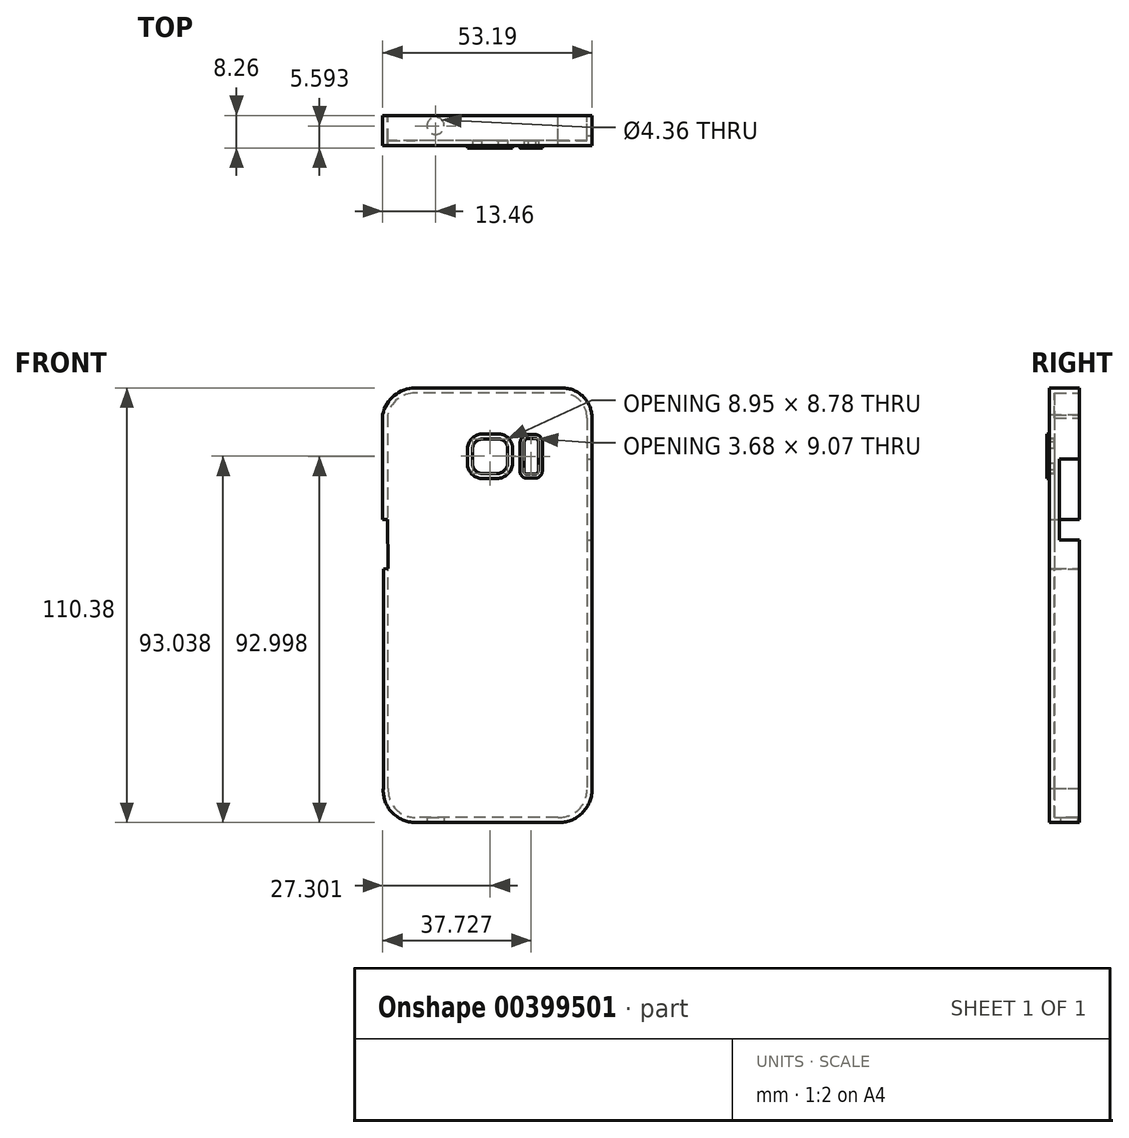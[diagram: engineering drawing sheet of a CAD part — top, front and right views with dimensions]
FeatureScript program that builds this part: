
annotation { "Feature Type Name" : "Feature", "Feature Type Description" : "" }
export const myFeature = defineFeature(function(context is Context, id is Id, definition is map)
    precondition{}
    {
        {
            var Q0;
            Q0=qCreatedBy(makeId("Front.planeOp"),FACE);
            var sketch = newSketch(context, id + "F0", { "sketchPlane" : qUnion([Q0])});
            skLineSegment(sketch, "E0", {"start": v(31.91, 44.57) * mm, "end": v(31.91, 34.16) * mm});
            skLineSegment(sketch, "E1", {"start": v(31.92, 13.5) * mm, "end": v(31.92, -49.87) * mm});
            skLineSegment(sketch, "E2", {"start": v(23.27, -58.16) * mm, "end": v(-12.99, -58.16) * mm});
            skLineSegment(sketch, "E3", {"start": v(-21.1, -49.5) * mm, "end": v(-21.1, 6.28) * mm});
            skLineSegment(sketch, "E4", {"start": v(24.35, 52.21) * mm, "end": v(-12.99, 52.21) * mm});
            skLineSegment(sketch, "E5", {"start": v(-21.27, 45.42) * mm, "end": v(-21.27, 18.78) * mm});
            skArc(sketch, "E6", {"start": v(24.35, 52.21) * mm, "mid": v(29.72, 49.97) * mm, "end": v(31.91, 44.57) * mm});
            skArc(sketch, "E7", {"start": v(-12.99, 52.21) * mm, "mid": v(-18.34, 50.3) * mm, "end": v(-21.27, 45.42) * mm});
            skArc(sketch, "E8", {"start": v(31.92, -49.87) * mm, "mid": v(29.36, -55.86) * mm, "end": v(23.27, -58.16) * mm});
            skArc(sketch, "E9", {"start": v(-12.99, -58.16) * mm, "mid": v(-18.92, -55.6) * mm, "end": v(-21.1, -49.5) * mm});
            skLineSegment(sketch, "E10", {"start": v(31.91, 34.16) * mm, "end": v(34.2, 34.16) * mm});
            skLineSegment(sketch, "E11.0", {"start": v(34.2, 44.56) * mm, "end": v(34.2, 34.16) * mm});
            skArc(sketch, "E11.1", {"start": v(24.35, 54.5) * mm, "mid": v(31.34, 51.58) * mm, "end": v(34.2, 44.56) * mm});
            skLineSegment(sketch, "E11.2", {"start": v(24.35, 54.5) * mm, "end": v(-12.99, 54.5) * mm});
            skArc(sketch, "E11.3", {"start": v(-12.99, 54.5) * mm, "mid": v(-19.88, 51.99) * mm, "end": v(-23.56, 45.64) * mm});
            skLineSegment(sketch, "E11.4", {"start": v(-23.56, 45.64) * mm, "end": v(-23.56, 18.78) * mm});
            skLineSegment(sketch, "E11.5", {"start": v(-21.27, 18.78) * mm, "end": v(-23.56, 18.78) * mm});
            skLineSegment(sketch, "E11.9", {"start": v(34.73, 24.26) * mm, "end": v(34.71, 24.26) * mm});
            skLineSegment(sketch, "E11.11", {"start": v(34.2, 13.5) * mm, "end": v(34.2, -49.87) * mm});
            skArc(sketch, "E11.12", {"start": v(34.2, -49.87) * mm, "mid": v(30.96, -57.5) * mm, "end": v(23.22, -60.45) * mm});
            skLineSegment(sketch, "E11.13", {"start": v(23.22, -60.45) * mm, "end": v(-12.99, -60.45) * mm});
            skArc(sketch, "E11.14", {"start": v(-12.99, -60.45) * mm, "mid": v(-20.56, -57.18) * mm, "end": v(-23.39, -49.43) * mm});
            skLineSegment(sketch, "E11.15", {"start": v(-23.39, -49.43) * mm, "end": v(-23.39, 6.28) * mm});
            skLineSegment(sketch, "E11.16", {"start": v(-23.39, 6.28) * mm, "end": v(-21.1, 6.28) * mm});
            skPoint(sketch, "E12.start.orphan", {"position": v(32.43, 15.78) * mm});
            skLineSegment(sketch, "E13", {"start": v(34.2, 13.5) * mm, "end": v(31.92, 13.5) * mm});
            skPoint(sketch, "E14.orphan", {"position": v(31.92, 15.78) * mm});
            skLineSegment(sketch, "E15", {"start": v(-23.56, 18.78) * mm, "end": v(-23.39, 6.28) * mm});
            skLineSegment(sketch, "E16", {"start": v(-21.27, 18.78) * mm, "end": v(-21.1, 6.28) * mm});
            skLineSegment(sketch, "E17", {"start": v(34.2, 34.16) * mm, "end": v(34.2, 13.5) * mm});
            skLineSegment(sketch, "E18", {"start": v(31.91, 34.16) * mm, "end": v(31.92, 13.5) * mm});
            skLineSegment(sketch, "E19", {"start": v(38.67, 39.3) * mm, "end": v(38.67, -10.21) * mm});
            skLineSegment(sketch, "E20", {"start": v(40.23, -10.83) * mm, "end": v(40.23, -26.24) * mm});
            skLineSegment(sketch, "E21", {"start": v(38.67, -10.21) * mm, "end": v(40.23, -10.83) * mm});
            skLineSegment(sketch, "E22", {"start": v(40.23, -26.24) * mm, "end": v(44.59, -30.44) * mm});
            skLineSegment(sketch, "E23", {"start": v(44.59, -30.44) * mm, "end": v(41.47, -62.98) * mm});
            skLineSegment(sketch, "E24", {"start": v(41.47, -62.98) * mm, "end": v(38.67, -62.98) * mm});
            skLineSegment(sketch, "E25", {"start": v(38.67, -62.98) * mm, "end": v(36.5, -64.85) * mm});
            skLineSegment(sketch, "E26", {"start": v(36.5, -64.85) * mm, "end": v(5.61, -64.85) * mm});
            skLineSegment(sketch, "E27", {"start": v(38.67, 39.3) * mm, "end": v(36.72, 49.13) * mm});
            skLineSegment(sketch, "E28", {"start": v(36.72, 49.13) * mm, "end": v(35, 49.13) * mm});
            skLineSegment(sketch, "E29.MirrorCS", {"start": v(-27.44, -62.98) * mm, "end": v(-25.26, -64.85) * mm});
            skLineSegment(sketch, "E30.MirrorCS", {"start": v(-30.25, -62.98) * mm, "end": v(-27.44, -62.98) * mm});
            skLineSegment(sketch, "E31.MirrorCS", {"start": v(-29, -26.24) * mm, "end": v(-33.36, -30.44) * mm});
            skLineSegment(sketch, "E32.MirrorCS", {"start": v(-27.44, 39.3) * mm, "end": v(-25.5, 49.13) * mm});
            skLineSegment(sketch, "E33.MirrorCS", {"start": v(-27.44, -10.21) * mm, "end": v(-29, -10.83) * mm});
            skLineSegment(sketch, "E34.MirrorCS", {"start": v(-25.5, 49.13) * mm, "end": v(-23.77, 49.13) * mm});
            skLineSegment(sketch, "E35.MirrorCS", {"start": v(-33.36, -30.44) * mm, "end": v(-30.25, -62.98) * mm});
            skLineSegment(sketch, "E36.MirrorCS", {"start": v(-27.44, 39.3) * mm, "end": v(-27.44, -10.21) * mm});
            skLineSegment(sketch, "E37.MirrorCS", {"start": v(-29, -10.83) * mm, "end": v(-29, -26.24) * mm});
            skLineSegment(sketch, "E38.MirrorCS", {"start": v(-25.26, -64.85) * mm, "end": v(5.61, -64.85) * mm});
            skSolve(sketch);
        }
        {
            var Q0;
            Q0=makeQuery(id+"F0.imprint","IMPRINT",FACE,{"disambiguationData":[TD([[makeQuery(id+"F0.imprint","IMPRINT",EDGE,{"derivedFrom":sQuery(id+"F0.wireOp",EDGE,"E0")}),-1.0]])]});
            extrude(context, id + "F1", {"entities" : qUnion([Q0]), "depth" : 7.62 * mm});
        }
        {
            var Q0;
            Q0=makeQuery(id+"F1.opExtrude","CAP_FACE",FACE,{"disambiguationData":[OSD([sQuery(id+"F0.wireOp",EDGE,"E0"),sQuery(id+"F0.wireOp",EDGE,"E1"),sQuery(id+"F0.wireOp",EDGE,"E2"),sQuery(id+"F0.wireOp",EDGE,"E3"),sQuery(id+"F0.wireOp",EDGE,"E4"),sQuery(id+"F0.wireOp",EDGE,"E5"),sQuery(id+"F0.wireOp",EDGE,"E6"),sQuery(id+"F0.wireOp",EDGE,"E7"),sQuery(id+"F0.wireOp",EDGE,"E8"),sQuery(id+"F0.wireOp",EDGE,"E9"),sQuery(id+"F0.wireOp",EDGE,"bb75414d-56e8-4ebf-947c-b1fa3df4ddbe.0"),sQuery(id+"F0.wireOp",EDGE,"bb75414d-56e8-4ebf-947c-b1fa3df4ddbe.1"),sQuery(id+"F0.wireOp",EDGE,"bb75414d-56e8-4ebf-947c-b1fa3df4ddbe.2"),sQuery(id+"F0.wireOp",EDGE,"bb75414d-56e8-4ebf-947c-b1fa3df4ddbe.3"),sQuery(id+"F0.wireOp",EDGE,"bb75414d-56e8-4ebf-947c-b1fa3df4ddbe.4"),sQuery(id+"F0.wireOp",EDGE,"bb75414d-56e8-4ebf-947c-b1fa3df4ddbe.5"),sQuery(id+"F0.wireOp",EDGE,"bb75414d-56e8-4ebf-947c-b1fa3df4ddbe.6"),sQuery(id+"F0.wireOp",EDGE,"bb75414d-56e8-4ebf-947c-b1fa3df4ddbe.7"),sQuery(id+"F0.wireOp",EDGE,"35a4204d-8211-4e34-a5d2-bb70df10542c.0"),sQuery(id+"F0.wireOp",EDGE,"35a4204d-8211-4e34-a5d2-bb70df10542c.1"),sQuery(id+"F0.wireOp",EDGE,"35a4204d-8211-4e34-a5d2-bb70df10542c.2"),sQuery(id+"F0.wireOp",EDGE,"35a4204d-8211-4e34-a5d2-bb70df10542c.3"),sQuery(id+"F0.wireOp",EDGE,"35a4204d-8211-4e34-a5d2-bb70df10542c.4"),sQuery(id+"F0.wireOp",EDGE,"35a4204d-8211-4e34-a5d2-bb70df10542c.5"),sQuery(id+"F0.wireOp",EDGE,"35a4204d-8211-4e34-a5d2-bb70df10542c.6"),sQuery(id+"F0.wireOp",EDGE,"35a4204d-8211-4e34-a5d2-bb70df10542c.7"),sQuery(id+"F0.wireOp",EDGE,"E16"),sQuery(id+"F0.wireOp",EDGE,"E18")])],"isStart":true});
            shell(context, id + "F2", {"entities" : qUnion([Q0]), "thickness" : 1.27 * mm});
        }
        {
            var Q0;
            Q0=makeQuery(id+"F1.opExtrude","SWEPT_FACE",FACE,{"disambiguationData":[OSD([sQuery(id+"F0.wireOp",EDGE,"E16")])]});
            cPlane(context, id + "F3", {"entities" : qUnion([Q0]), "cplaneType" : CPlaneType.OFFSET, "offset" : 0 * mm, "width" : 152.4 * mm, "height" : 152.4 * mm});
        }
        {
            var Q0;
            Q0=makeQuery(id+"F1.opExtrude","SWEPT_FACE",FACE,{"disambiguationData":[OSD([sQuery(id+"F0.wireOp",EDGE,"E16")])]});
            extrude(context, id + "F4", {"entities" : qUnion([Q0]), "operationType" : NewBodyOperationType.REMOVE, "oppositeDirection" : true, "depth" : 1.27 * mm});
        }
        {
            var Q0;
            Q0=makeQuery(id+"F1.opExtrude","SWEPT_FACE",FACE,{"disambiguationData":[OSD([sQuery(id+"F0.wireOp",EDGE,"E18")])]});
            cPlane(context, id + "F5", {"entities" : qUnion([Q0]), "cplaneType" : CPlaneType.OFFSET, "offset" : 0 * mm, "width" : 152.4 * mm, "height" : 152.4 * mm});
        }
        {
            var Q0;
            Q0=qCreatedBy(id+"F5.planeOp",FACE);
            var sketch = newSketch(context, id + "F6", { "sketchPlane" : qUnion([Q0])});
            skLineSegment(sketch, "E39.bottom", {"start": v(-5.1, 34.2) * mm, "end": v(0, 34.2) * mm});
            skLineSegment(sketch, "E39.top", {"start": v(-5.1, 13.52) * mm, "end": v(0, 13.52) * mm});
            skLineSegment(sketch, "E39.left", {"start": v(-5.1, 34.2) * mm, "end": v(-5.1, 13.52) * mm});
            skLineSegment(sketch, "E39.right", {"start": v(0, 34.2) * mm, "end": v(0, 13.52) * mm});
            skSolve(sketch);
        }
        {
            var Q0;
            Q0=makeQuery(id+"F6.imprint","IMPRINT",FACE,{"disambiguationData":[TD([[makeQuery(id+"F6.imprint","IMPRINT",EDGE,{"derivedFrom":sQuery(id+"F6.wireOp",EDGE,"E39.bottom")}),-1.0]])]});
            extrude(context, id + "F7", {"entities" : qUnion([Q0]), "operationType" : NewBodyOperationType.REMOVE, "oppositeDirection" : true, "depth" : 1.27 * mm});
        }
        {
            var Q0;
            Q0=makeQuery(id+"F1.opExtrude","CAP_FACE",FACE,{"disambiguationData":[OSD([sQuery(id+"F0.wireOp",EDGE,"E0"),sQuery(id+"F0.wireOp",EDGE,"E1"),sQuery(id+"F0.wireOp",EDGE,"E2"),sQuery(id+"F0.wireOp",EDGE,"E3"),sQuery(id+"F0.wireOp",EDGE,"E4"),sQuery(id+"F0.wireOp",EDGE,"E5"),sQuery(id+"F0.wireOp",EDGE,"E6"),sQuery(id+"F0.wireOp",EDGE,"E7"),sQuery(id+"F0.wireOp",EDGE,"E8"),sQuery(id+"F0.wireOp",EDGE,"E9"),sQuery(id+"F0.wireOp",EDGE,"E16"),sQuery(id+"F0.wireOp",EDGE,"E18")])],"isStart":false});
            var sketch = newSketch(context, id + "F8", { "sketchPlane" : qUnion([Q0])});
            skLineSegment(sketch, "E40", {"start": v(8.03, 39.26) * mm, "end": v(4.22, 39.26) * mm});
            skLineSegment(sketch, "E41", {"start": v(7.72, 30.48) * mm, "end": v(3.9, 30.48) * mm});
            skLineSegment(sketch, "E42", {"start": v(10.5, 36.85) * mm, "end": v(10.5, 33.03) * mm});
            skLineSegment(sketch, "E43", {"start": v(1.56, 36.84) * mm, "end": v(1.56, 33.02) * mm});
            skArc(sketch, "E44", {"start": v(4.22, 39.26) * mm, "mid": v(2.42, 38.56) * mm, "end": v(1.56, 36.84) * mm});
            skArc(sketch, "E45", {"start": v(1.56, 33.02) * mm, "mid": v(2.23, 31.3) * mm, "end": v(3.9, 30.48) * mm});
            skArc(sketch, "E46", {"start": v(7.72, 30.48) * mm, "mid": v(9.6, 31.21) * mm, "end": v(10.5, 33.03) * mm});
            skArc(sketch, "E47", {"start": v(10.5, 36.85) * mm, "mid": v(9.78, 38.57) * mm, "end": v(8.03, 39.26) * mm});
            skArc(sketch, "E48.0", {"start": v(4.22, 40.53) * mm, "mid": v(1.54, 39.48) * mm, "end": v(0.29, 36.9) * mm});
            skLineSegment(sketch, "E48.1", {"start": v(8.02, 40.53) * mm, "end": v(4.22, 40.53) * mm});
            skLineSegment(sketch, "E48.2", {"start": v(0.29, 36.9) * mm, "end": v(0.29, 33.02) * mm});
            skArc(sketch, "E48.3", {"start": v(11.77, 36.85) * mm, "mid": v(10.67, 39.48) * mm, "end": v(8.02, 40.53) * mm});
            skArc(sketch, "E48.4", {"start": v(0.29, 33.02) * mm, "mid": v(1.32, 30.41) * mm, "end": v(3.86, 29.2) * mm});
            skLineSegment(sketch, "E48.5", {"start": v(7.72, 29.2) * mm, "end": v(3.86, 29.2) * mm});
            skArc(sketch, "E48.6", {"start": v(7.72, 29.2) * mm, "mid": v(10.49, 30.3) * mm, "end": v(11.77, 32.98) * mm});
            skLineSegment(sketch, "E48.7", {"start": v(11.77, 36.85) * mm, "end": v(11.77, 32.98) * mm});
            skLineSegment(sketch, "E49", {"start": v(14.69, 38.33) * mm, "end": v(14.69, 31.43) * mm});
            skLineSegment(sketch, "E50", {"start": v(18.3, 38.43) * mm, "end": v(18.3, 31.22) * mm});
            skLineSegment(sketch, "E51", {"start": v(15.41, 30.3) * mm, "end": v(17.58, 30.3) * mm});
            skLineSegment(sketch, "E52", {"start": v(15.62, 39.36) * mm, "end": v(17.47, 39.36) * mm});
            skArc(sketch, "E53", {"start": v(14.69, 38.33) * mm, "mid": v(14.96, 39.03) * mm, "end": v(15.62, 39.36) * mm});
            skArc(sketch, "E54", {"start": v(17.47, 39.36) * mm, "mid": v(18.1, 39.08) * mm, "end": v(18.3, 38.43) * mm});
            skArc(sketch, "E55", {"start": v(18.3, 31.22) * mm, "mid": v(18.1, 30.63) * mm, "end": v(17.58, 30.3) * mm});
            skArc(sketch, "E56", {"start": v(15.41, 30.3) * mm, "mid": v(14.74, 30.66) * mm, "end": v(14.69, 31.43) * mm});
            skArc(sketch, "E57.0", {"start": v(13.67, 38.33) * mm, "mid": v(14.22, 39.73) * mm, "end": v(15.57, 40.38) * mm});
            skLineSegment(sketch, "E57.1", {"start": v(15.57, 40.38) * mm, "end": v(17.47, 40.38) * mm});
            skLineSegment(sketch, "E57.2", {"start": v(13.67, 38.33) * mm, "end": v(13.67, 31.6) * mm});
            skArc(sketch, "E57.3", {"start": v(17.47, 40.38) * mm, "mid": v(18.83, 39.79) * mm, "end": v(19.31, 38.39) * mm});
            skArc(sketch, "E57.4", {"start": v(15.41, 29.28) * mm, "mid": v(13.96, 30) * mm, "end": v(13.67, 31.6) * mm});
            skLineSegment(sketch, "E57.5", {"start": v(15.41, 29.28) * mm, "end": v(17.68, 29.28) * mm});
            skArc(sketch, "E57.6", {"start": v(19.31, 31.22) * mm, "mid": v(18.85, 29.95) * mm, "end": v(17.68, 29.28) * mm});
            skLineSegment(sketch, "E57.7", {"start": v(19.31, 38.39) * mm, "end": v(19.31, 31.22) * mm});
            skSolve(sketch);
        }
        {
            var Q0;
            Q0 = qSketchRegion(id + "F8", true);
            extrude(context, id + "F9", {"entities" : qUnion([Q0]), "operationType" : NewBodyOperationType.ADD, "endBound" : BoundingType.SYMMETRIC, "oppositeDirection" : true, "depth" : 1.27 * mm});
        }
        {
            var Q0;
            Q0=makeQuery(id+"F9.boolean.opBoolean","SPLIT",FACE,{"disambiguationData":[TD([makeQuery(id+"F9.opExtrude","SWEPT_FACE",FACE,{"disambiguationData":[OSD([sQuery(id+"F8.wireOp",EDGE,"E49")])]})])],"derivedFrom":makeQuery(id+"F1.opExtrude","CAP_FACE",FACE,{"disambiguationData":[OSD([sQuery(id+"F0.wireOp",EDGE,"E0"),sQuery(id+"F0.wireOp",EDGE,"E1"),sQuery(id+"F0.wireOp",EDGE,"E2"),sQuery(id+"F0.wireOp",EDGE,"E3"),sQuery(id+"F0.wireOp",EDGE,"E4"),sQuery(id+"F0.wireOp",EDGE,"E5"),sQuery(id+"F0.wireOp",EDGE,"E6"),sQuery(id+"F0.wireOp",EDGE,"E7"),sQuery(id+"F0.wireOp",EDGE,"E8"),sQuery(id+"F0.wireOp",EDGE,"E9"),sQuery(id+"F0.wireOp",EDGE,"E16"),sQuery(id+"F0.wireOp",EDGE,"E18")])],"isStart":false})});
            var Q1;
            Q1=makeQuery(id+"F9.boolean.opBoolean","SPLIT",FACE,{"disambiguationData":[TD([makeQuery(id+"F9.opExtrude","SWEPT_FACE",FACE,{"disambiguationData":[OSD([sQuery(id+"F8.wireOp",EDGE,"E40")])]})])],"derivedFrom":makeQuery(id+"F1.opExtrude","CAP_FACE",FACE,{"disambiguationData":[OSD([sQuery(id+"F0.wireOp",EDGE,"E0"),sQuery(id+"F0.wireOp",EDGE,"E1"),sQuery(id+"F0.wireOp",EDGE,"E2"),sQuery(id+"F0.wireOp",EDGE,"E3"),sQuery(id+"F0.wireOp",EDGE,"E4"),sQuery(id+"F0.wireOp",EDGE,"E5"),sQuery(id+"F0.wireOp",EDGE,"E6"),sQuery(id+"F0.wireOp",EDGE,"E7"),sQuery(id+"F0.wireOp",EDGE,"E8"),sQuery(id+"F0.wireOp",EDGE,"E9"),sQuery(id+"F0.wireOp",EDGE,"E16"),sQuery(id+"F0.wireOp",EDGE,"E18")])],"isStart":false})});
            extrude(context, id + "F10", {"entities" : qUnion([Q0, Q1]), "operationType" : NewBodyOperationType.REMOVE, "oppositeDirection" : true, "depth" : 25.4 * mm});
        }
        {
            var Q0;
            Q0=makeQuery(id+"F1.opExtrude","SWEPT_FACE",FACE,{"disambiguationData":[OSD([sQuery(id+"F0.wireOp",EDGE,"E2")])]});
            cPlane(context, id + "F11", {"entities" : qUnion([Q0]), "cplaneType" : CPlaneType.OFFSET, "offset" : 0 * mm, "width" : 152.4 * mm, "height" : 152.4 * mm});
        }
        {
            var Q0;
            Q0=qCreatedBy(id+"F11.planeOp",FACE);
            var sketch = newSketch(context, id + "F12", { "sketchPlane" : qUnion([Q0])});
            skLineSegment(sketch, "E58.bottom", {"start": v(3.06, 5.59) * mm, "end": v(9.82, 5.59) * mm});
            skLineSegment(sketch, "E58.left", {"start": v(2, 4.58) * mm, "end": v(2, 1.76) * mm});
            skLineSegment(sketch, "E59.bottom", {"start": v(16.78, 5.3) * mm, "end": v(21.78, 5.3) * mm});
            skLineSegment(sketch, "E59.left", {"start": v(15.88, 4.62) * mm, "end": v(15.88, 2.31) * mm});
            skCircle(sketch, "E60", {"center": v(-7.81, 2.67) * mm, "radius": 2.18 * mm});
            skArc(sketch, "E61", {"start": v(2, 4.58) * mm, "mid": v(2.31, 5.3) * mm, "end": v(3.06, 5.59) * mm});
            skPoint(sketch, "E62.orphan", {"position": v(22.32, 1.76) * mm});
            skArc(sketch, "E63", {"start": v(15.88, 4.62) * mm, "mid": v(16.16, 5.18) * mm, "end": v(16.78, 5.3) * mm});
            skLineSegment(sketch, "E64.MirrorCS", {"start": v(21.78, 5.3) * mm, "end": v(16.78, 5.3) * mm});
            skArc(sketch, "E65.MirrorCS", {"start": v(22.68, 4.62) * mm, "mid": v(22.4, 5.18) * mm, "end": v(21.78, 5.3) * mm});
            skLineSegment(sketch, "E66.MirrorCS", {"start": v(22.68, 4.62) * mm, "end": v(22.68, 2.31) * mm});
            skPoint(sketch, "E67.orphan", {"position": v(19.28, 5.3) * mm});
            skLineSegment(sketch, "E68.MirrorCS", {"start": v(16.78, 1.63) * mm, "end": v(21.78, 1.63) * mm});
            skArc(sketch, "E69.MirrorCS", {"start": v(15.88, 2.31) * mm, "mid": v(16.16, 1.75) * mm, "end": v(16.78, 1.63) * mm});
            skLineSegment(sketch, "E70.MirrorCS", {"start": v(15.88, 2.31) * mm, "end": v(15.88, 4.62) * mm});
            skArc(sketch, "E71.MirrorCS", {"start": v(22.68, 2.31) * mm, "mid": v(22.4, 1.75) * mm, "end": v(21.78, 1.63) * mm});
            skLineSegment(sketch, "E72.MirrorCS", {"start": v(22.68, 2.31) * mm, "end": v(22.68, 4.62) * mm});
            skPoint(sketch, "E73.start.orphan", {"position": v(16.78, 1.76) * mm});
            skPoint(sketch, "E74.end.orphan", {"position": v(22.68, 3.47) * mm});
            skPoint(sketch, "E74.start.orphan", {"position": v(15.88, 3.47) * mm});
            skLineSegment(sketch, "E75.MirrorCS", {"start": v(3.06, 0.75) * mm, "end": v(9.82, 0.75) * mm});
            skArc(sketch, "E76.MirrorCS", {"start": v(2, 1.76) * mm, "mid": v(2.31, 1.03) * mm, "end": v(3.06, 0.75) * mm});
            skLineSegment(sketch, "E77.MirrorCS", {"start": v(2, 1.76) * mm, "end": v(2, 4.58) * mm});
            skLineSegment(sketch, "E78.MirrorCS", {"start": v(9.82, 5.59) * mm, "end": v(3.06, 5.59) * mm});
            skArc(sketch, "E79.MirrorCS", {"start": v(10.88, 4.58) * mm, "mid": v(10.57, 5.3) * mm, "end": v(9.82, 5.59) * mm});
            skLineSegment(sketch, "E80.MirrorCS", {"start": v(10.88, 4.58) * mm, "end": v(10.88, 1.76) * mm});
            skArc(sketch, "E81.MirrorCS", {"start": v(10.88, 1.76) * mm, "mid": v(10.57, 1.03) * mm, "end": v(9.82, 0.75) * mm});
            skLineSegment(sketch, "E82.MirrorCS", {"start": v(9.82, 0.75) * mm, "end": v(3.06, 0.75) * mm});
            skPoint(sketch, "E83.orphan", {"position": v(6.44, 5.59) * mm});
            skPoint(sketch, "E84.end.orphan", {"position": v(6.44, 0.82) * mm});
            skPoint(sketch, "E85.start.orphan", {"position": v(2, 3.17) * mm});
            skSolve(sketch);
        }
        {
            var Q0;
            Q0=makeQuery(id+"F12.imprint","IMPRINT",FACE,{"disambiguationData":[TD([[makeQuery(id+"F12.imprint","IMPRINT",EDGE,{"derivedFrom":sQuery(id+"F12.wireOp",EDGE,"E60")}),1.0]])]});
            var Q1;
            Q1=makeQuery(id+"F12.imprint","IMPRINT",FACE,{"disambiguationData":[TD([[makeQuery(id+"F12.imprint","IMPRINT",EDGE,{"derivedFrom":sQuery(id+"F12.wireOp",EDGE,"E61")}),-1.0]])]});
            var Q2;
            Q2=makeQuery(id+"F12.imprint","IMPRINT",FACE,{"disambiguationData":[TD([[makeQuery(id+"F12.imprint","IMPRINT",EDGE,{"derivedFrom":sQuery(id+"F12.wireOp",EDGE,"E63")}),-1.0]])]});
            extrude(context, id + "F13", {"entities" : qUnion([Q0, Q1, Q2]), "operationType" : NewBodyOperationType.REMOVE, "oppositeDirection" : true, "depth" : 1.27 * mm});
        }
    });
